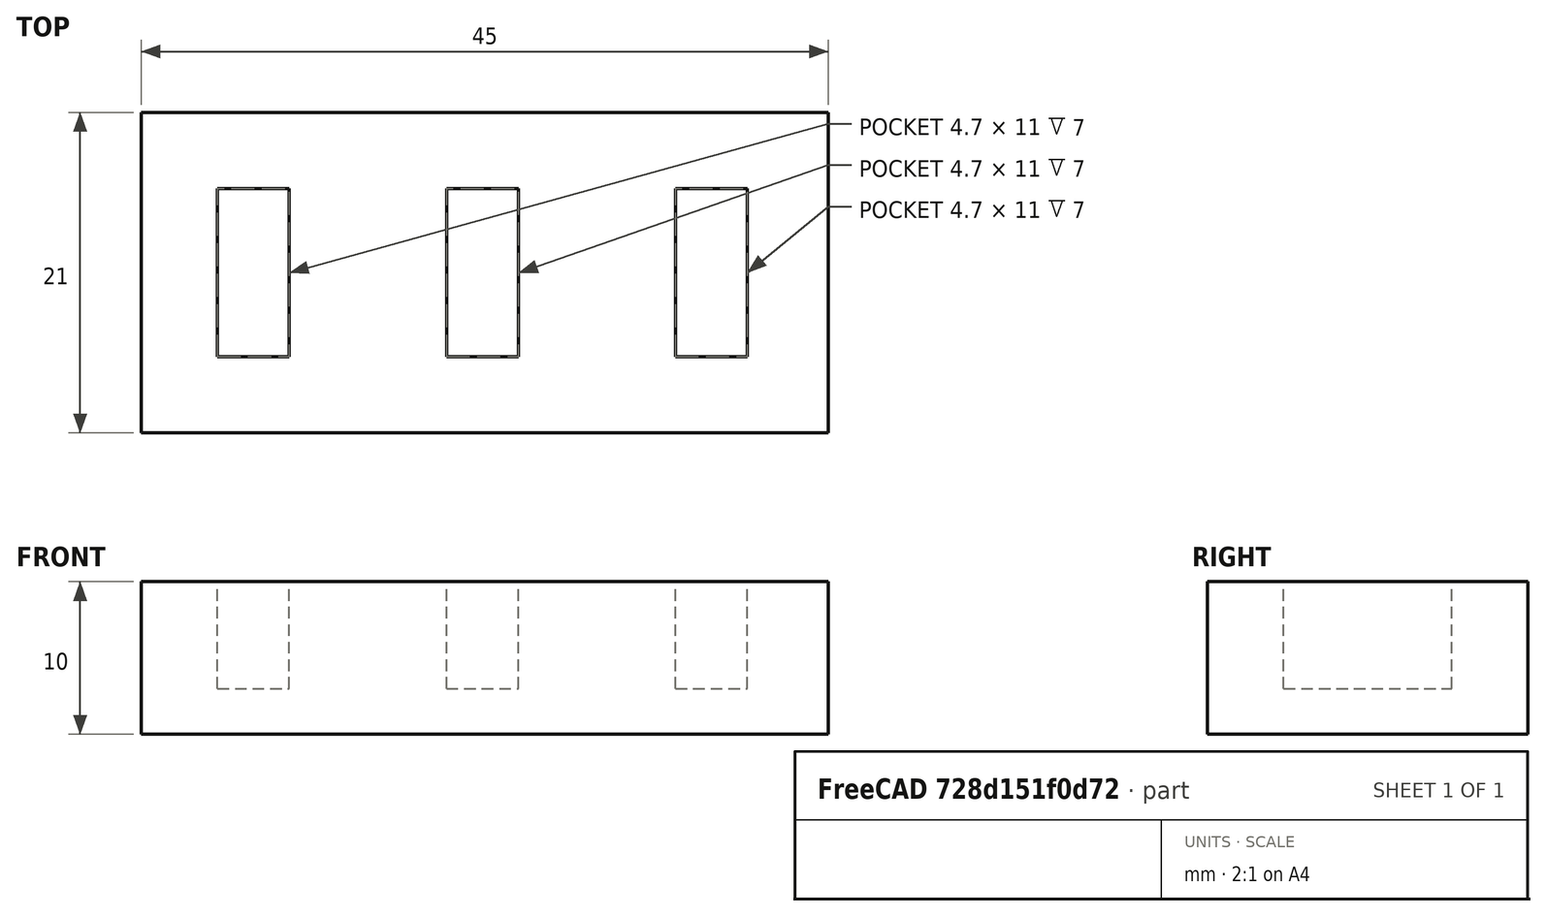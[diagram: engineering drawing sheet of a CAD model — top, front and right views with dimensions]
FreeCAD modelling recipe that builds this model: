
FCSTD DOCUMENT  (FreeCAD 1.0R39285 (Git))
Label: ojt1_t08p01_USB_flash
License: All rights reserved
objects: Part::Box×4, Part::MultiFuse×1, Part::Cut×1
note: 6 computed .brp shape members not serialized (recipe doc carries the construction recipe); baked Part::Feature solids carry a one-line shape summary decoded from their .brp

FEATURE [Part::Box] Box  label="slot"
  AttacherType = Attacher::AttachEngine3D
  Height = 12
  Length = 4.7
  Width = 11
FEATURE [Part::Box] Box001  label="slot001"
  AttacherType = Attacher::AttachEngine3D
  Height = 12
  Length = 4.7
  Placement = pos=(15,0,0) rot=(0,0,1;0rad)
  Width = 11
FEATURE [Part::Box] Box002  label="slot002"
  AttacherType = Attacher::AttachEngine3D
  Height = 12
  Length = 4.7
  Placement = pos=(30,0,0) rot=(0,0,1;0rad)
  Width = 11
FEATURE [Part::Box] Box003  label="basis"
  AttacherType = Attacher::AttachEngine3D
  Height = 10
  Length = 45
  Width = 21
FEATURE [Part::MultiFuse] Fusion  label="slots"
  Placement = pos=(5,5,3) rot=(0,0,1;0rad)
  Refine = true
  Shapes = -> [Box,Box001,Box002]
FEATURE [Part::Cut] Cut
  Base = -> Box003
  Refine = true
  Tool = -> Fusion
